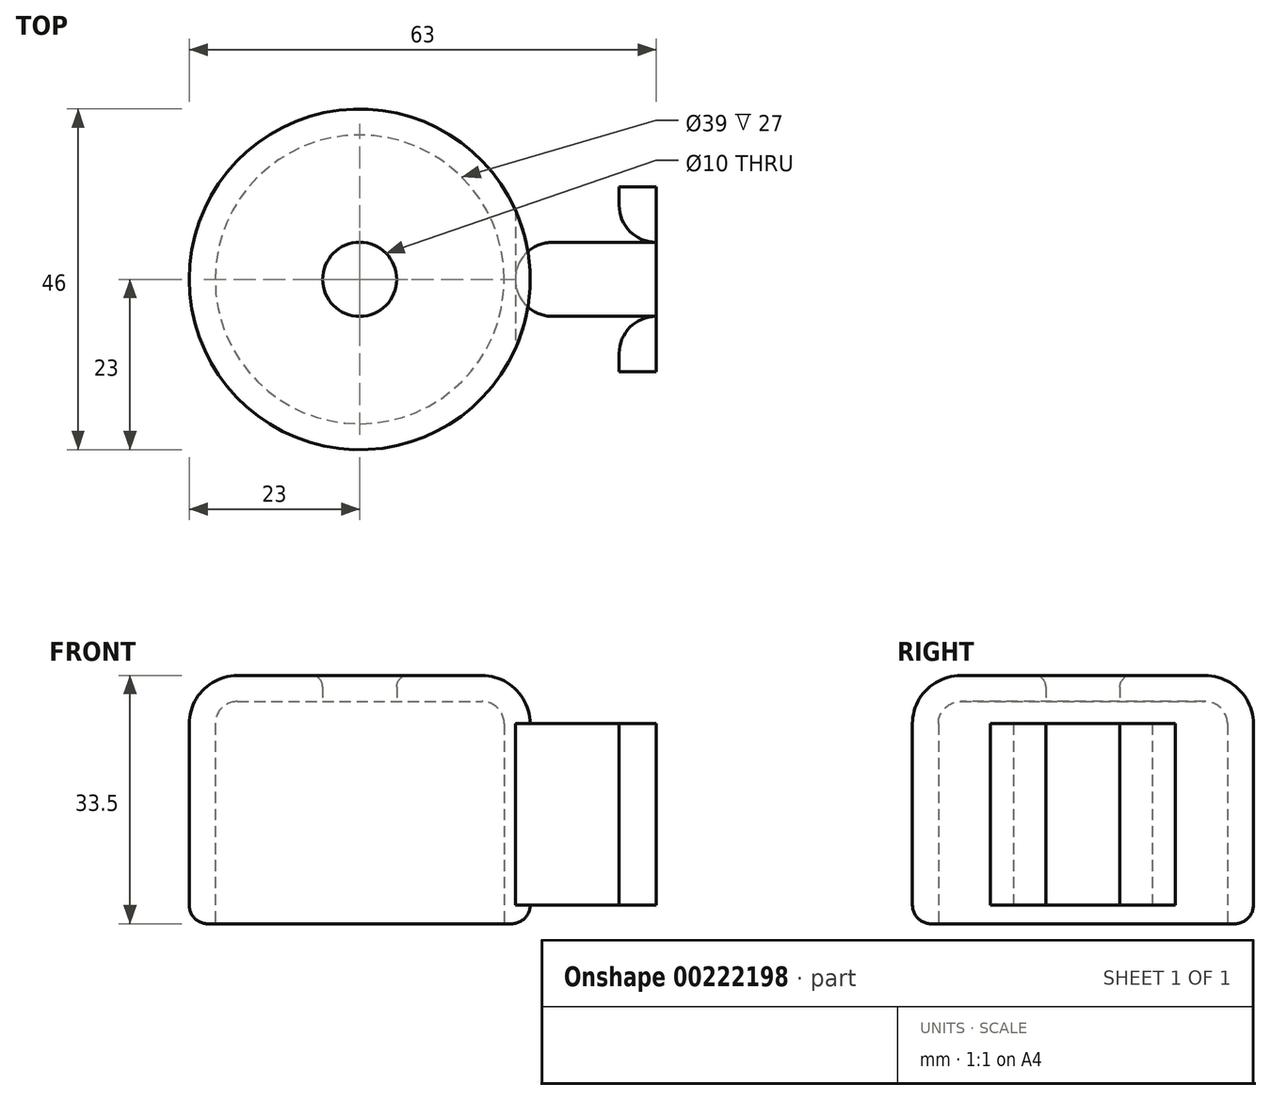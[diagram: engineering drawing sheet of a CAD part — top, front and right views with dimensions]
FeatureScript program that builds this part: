
annotation { "Feature Type Name" : "Feature", "Feature Type Description" : "" }
export const myFeature = defineFeature(function(context is Context, id is Id, definition is map)
    precondition{}
    {
        {
            var Q0;
            Q0=qCreatedBy(makeId("Front.planeOp"),FACE);
            var sketch = newSketch(context, id + "F0", { "sketchPlane" : qUnion([Q0])});
            skLineSegment(sketch, "E0", {"start": v(5, 9.95) * mm, "end": v(16.5, 9.95) * mm});
            skLineSegment(sketch, "E1", {"start": v(19.5, 6.95) * mm, "end": v(19.5, -20.05) * mm});
            skPoint(sketch, "E2.visualSharp", {"position": v(19.5, 9.95) * mm});
            skArc(sketch, "E2.filletArc", {"start": v(19.5, 6.95) * mm, "mid": v(18.62, 9.07) * mm, "end": v(16.5, 9.95) * mm});
            skLineSegment(sketch, "E3.0", {"start": v(23, 6.95) * mm, "end": v(23, -17.55) * mm});
            skArc(sketch, "E3.1", {"start": v(23, 6.95) * mm, "mid": v(21.1, 11.55) * mm, "end": v(16.5, 13.45) * mm});
            skLineSegment(sketch, "E3.2", {"start": v(6.5, 13.45) * mm, "end": v(16.5, 13.45) * mm});
            skLineSegment(sketch, "E4", {"start": v(19.5, -20.05) * mm, "end": v(20.5, -20.05) * mm});
            skLineSegment(sketch, "E5", {"start": v(0, 9.95) * mm, "end": v(0, 13.45) * mm});
            skPoint(sketch, "E6.visualSharp", {"position": v(23, -20.05) * mm});
            skArc(sketch, "E6.filletArc", {"start": v(20.5, -20.05) * mm, "mid": v(22.27, -19.32) * mm, "end": v(23, -17.55) * mm});
            skLineSegment(sketch, "E7", {"start": v(5, 9.95) * mm, "end": v(5, 11.95) * mm});
            skPoint(sketch, "E8.visualSharp", {"position": v(5, 13.45) * mm});
            skArc(sketch, "E8.filletArc", {"start": v(6.5, 13.45) * mm, "mid": v(5.44, 13.01) * mm, "end": v(5, 11.95) * mm});
            skSolve(sketch);
        }
        {
            var Q0;
            Q0=makeQuery(id+"F0.imprint","IMPRINT",FACE,{"disambiguationData":[TD([[makeQuery(id+"F0.imprint","IMPRINT",EDGE,{"derivedFrom":sQuery(id+"F0.wireOp",EDGE,"E0")}),1.0]])]});
            var Q1;
            Q1=sQuery(id+"F0.wireOp",EDGE,"E5");
            revolve(context, id + "F1", {"entities" : qUnion([Q0]), "axis" : qUnion([Q1]), "revolveType" : RevolveType.FULL});
        }
        {
            var Q0;
            Q0=qCreatedBy(makeId("Right.planeOp"),FACE);
            cPlane(context, id + "F2", {"entities" : qUnion([Q0]), "cplaneType" : CPlaneType.OFFSET, "offset" : 21 * mm, "width" : 150 * mm, "height" : 150 * mm});
        }
        {
            var Q0;
            Q0=qCreatedBy(id+"F2.planeOp",FACE);
            var sketch = newSketch(context, id + "F3", { "sketchPlane" : qUnion([Q0])});
            skLineSegment(sketch, "E9", {"start": v(-12.5, 7) * mm, "end": v(0, 7) * mm});
            skLineSegment(sketch, "E10", {"start": v(-12.5, -17.5) * mm, "end": v(-12.5, 7) * mm});
            skLineSegment(sketch, "E11", {"start": v(-5, 7) * mm, "end": v(-5, -17.5) * mm});
            skLineSegment(sketch, "E12", {"start": v(-5, -17.5) * mm, "end": v(0, -17.5) * mm});
            skLineSegment(sketch, "E13", {"start": v(0, -17.5) * mm, "end": v(0, 7) * mm});
            skLineSegment(sketch, "E14.trimOffspring", {"start": v(0, -17.5) * mm, "end": v(-12.5, -17.5) * mm});
            skPoint(sketch, "E15", {"position": v(-8.25, 2) * mm});
            skPoint(sketch, "E16", {"position": v(-8.25, -12.5) * mm});
            skLineSegment(sketch, "E17.MirrorCS", {"start": v(5, -17.5) * mm, "end": v(0, -17.5) * mm});
            skLineSegment(sketch, "E18.MirrorCS", {"start": v(12.5, -17.5) * mm, "end": v(12.5, 7) * mm});
            skLineSegment(sketch, "E19.MirrorCS", {"start": v(5, 7) * mm, "end": v(5, -17.5) * mm});
            skPoint(sketch, "E20.MirrorP", {"position": v(8.25, -12.5) * mm});
            skPoint(sketch, "E21.MirrorP", {"position": v(8.25, 2) * mm});
            skLineSegment(sketch, "E22.MirrorCS", {"start": v(0, -17.5) * mm, "end": v(12.5, -17.5) * mm});
            skLineSegment(sketch, "E23.MirrorCS", {"start": v(12.5, 7) * mm, "end": v(0, 7) * mm});
            skSolve(sketch);
        }
        {
            var Q0;
            {var subQ0=sQuery(id+"F3.wireOp",EDGE,"E10");Q0=makeQuery(id+"F3.imprint","IMPRINT",FACE,{"disambiguationData":[TD([[makeQuery(id+"F3.imprint","IMPRINT",EDGE,{"derivedFrom":subQ0}),-1.0]])]});}
            var Q1;
            {var subQ0=sQuery(id+"F3.wireOp",EDGE,"E18.MirrorCS");Q1=makeQuery(id+"F3.imprint","IMPRINT",FACE,{"disambiguationData":[TD([[makeQuery(id+"F3.imprint","IMPRINT",EDGE,{"derivedFrom":subQ0}),1.0]])]});}
            extrude(context, id + "F4", {"entities" : qUnion([Q0, Q1]), "operationType" : NewBodyOperationType.ADD, "depth" : 19 * mm});
        }
        {
            var Q0;
            Q0 = qSketchRegion(id + "F3", true);
            extrude(context, id + "F5", {"entities" : qUnion([Q0]), "operationType" : NewBodyOperationType.REMOVE, "depth" : 14 * mm});
        }
        {
            var Q0;
            {var subQ2=sQuery(id+"F3.wireOp",EDGE,"E11");Q0=makeQuery(id+"F3.imprint","IMPRINT",FACE,{"disambiguationData":[TD([[makeQuery(id+"F3.imprint","IMPRINT",EDGE,{"derivedFrom":subQ2}),1.0]])]});}
            var Q1;
            {var subQ0=sQuery(id+"F3.wireOp",EDGE,"E13");Q1=makeQuery(id+"F3.imprint","IMPRINT",FACE,{"disambiguationData":[TD([[makeQuery(id+"F3.imprint","IMPRINT",EDGE,{"derivedFrom":subQ0}),-1.0]])]});}
            extrude(context, id + "F6", {"entities" : qUnion([Q0, Q1]), "depth" : 19 * mm});
        }
        {
            var Q0;
            Q0=makeQuery(id+"F5.boolean.opBoolean","INTERSECT",EDGE,{"derivedFrom":[makeQuery(id+"F4.opExtrude","SWEPT_FACE",FACE,{"disambiguationData":[OSD([sQuery(id+"F3.wireOp",EDGE,"E19.MirrorCS")])]}),makeQuery(id+"F5.opExtrude","CAP_FACE",FACE,{"disambiguationData":[OSD([sQuery(id+"F3.wireOp",EDGE,"E9"),sQuery(id+"F3.wireOp",EDGE,"E10"),sQuery(id+"F3.wireOp",EDGE,"E14.trimOffspring"),sQuery(id+"F3.wireOp",EDGE,"E18.MirrorCS"),sQuery(id+"F3.wireOp",EDGE,"E22.MirrorCS"),sQuery(id+"F3.wireOp",EDGE,"E23.MirrorCS")])],"isStart":false})]});
            var Q1;
            Q1=makeQuery(id+"F5.boolean.opBoolean","INTERSECT",EDGE,{"derivedFrom":[makeQuery(id+"F4.opExtrude","SWEPT_FACE",FACE,{"disambiguationData":[OSD([sQuery(id+"F3.wireOp",EDGE,"E11")])]}),makeQuery(id+"F5.opExtrude","CAP_FACE",FACE,{"disambiguationData":[OSD([sQuery(id+"F3.wireOp",EDGE,"E9"),sQuery(id+"F3.wireOp",EDGE,"E10"),sQuery(id+"F3.wireOp",EDGE,"E14.trimOffspring"),sQuery(id+"F3.wireOp",EDGE,"E18.MirrorCS"),sQuery(id+"F3.wireOp",EDGE,"E22.MirrorCS"),sQuery(id+"F3.wireOp",EDGE,"E23.MirrorCS")])],"isStart":false})]});
            var Q2;
            Q2=makeQuery(id+"F6.opExtrude","CAP_EDGE",EDGE,{"disambiguationData":[OSD([sQuery(id+"F3.wireOp",EDGE,"E11")])],"isStart":true});
            var Q3;
            Q3=makeQuery(id+"F6.opExtrude","CAP_EDGE",EDGE,{"disambiguationData":[OSD([sQuery(id+"F3.wireOp",EDGE,"E19.MirrorCS")])],"isStart":true});
            fillet(context, id + "F7", {"entities" : qUnion([Q0, Q1, Q2, Q3]), "radius" : 5 * mm, "tangentPropagation" : true, "allowEdgeOverflow" : false});
        }
        {
            var Q0;
            Q0=sQuery(id+"F3.wireOp",VERTEX,"E21.MirrorP");
            var Q1;
            Q1=sQuery(id+"F3.wireOp",VERTEX,"E20.MirrorP");
            var Q2;
            Q2=sQuery(id+"F3.wireOp",VERTEX,"E16");
            var Q3;
            Q3=sQuery(id+"F3.wireOp",VERTEX,"E15");
            var Q4;
            Q4=makeQuery(id+"F6.opExtrude","SWEPT_BODY",BODY,{"disambiguationData":[OSD([sQuery(id+"F3.wireOp",EDGE,"E9"),sQuery(id+"F3.wireOp",EDGE,"E11"),sQuery(id+"F3.wireOp",EDGE,"E14.trimOffspring"),sQuery(id+"F3.wireOp",EDGE,"E19.MirrorCS"),sQuery(id+"F3.wireOp",EDGE,"E22.MirrorCS"),sQuery(id+"F3.wireOp",EDGE,"E23.MirrorCS")])]});
            hole(context, id + "F8", {"style" : HoleStyle.SIMPLE, "endStyle" : HoleEndStyle.THROUGH, "oppositeDirection" : true, "holeDiameter" : 3 * mm, "isTappedThrough" : true, "tappedDepth" : 12 * mm, "tapClearance" : 3, "startFromSketch" : true, "locations" : qUnion([Q0, Q1, Q2, Q3]), "scope" : qUnion([Q4])});
        }
    });
